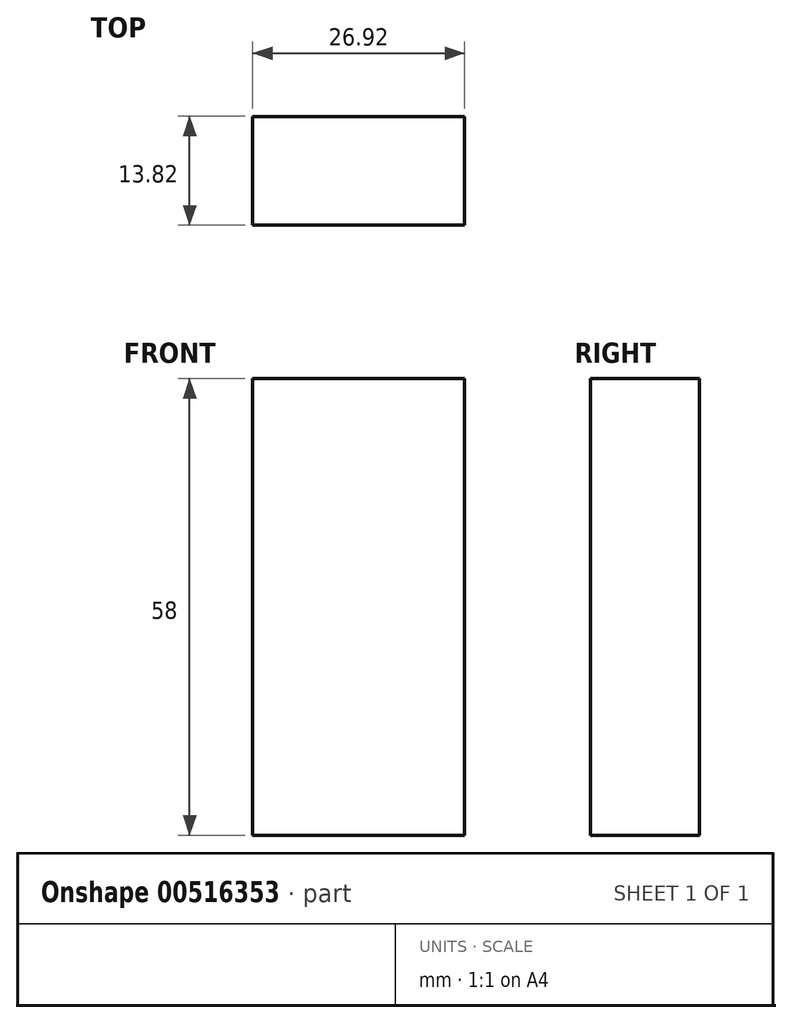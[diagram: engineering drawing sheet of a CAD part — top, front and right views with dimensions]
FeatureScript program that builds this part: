
annotation { "Feature Type Name" : "Feature", "Feature Type Description" : "" }
export const myFeature = defineFeature(function(context is Context, id is Id, definition is map)
    precondition{}
    {
        {
            var Q0;
            Q0=qCreatedBy(makeId("Top.planeOp"),FACE);
            var sketch = newSketch(context, id + "F0", { "sketchPlane" : qUnion([Q0])});
            skLineSegment(sketch, "E0.bottom", {"start": v(-34.73, 27.33) * mm, "end": v(-18.21, 27.33) * mm});
            skLineSegment(sketch, "E0.top", {"start": v(-34.73, -25.16) * mm, "end": v(-18.21, -25.16) * mm});
            skLineSegment(sketch, "E0.left", {"start": v(-34.73, 27.33) * mm, "end": v(-34.73, -25.16) * mm});
            skLineSegment(sketch, "E0.right", {"start": v(-18.21, 27.33) * mm, "end": v(-18.21, -25.16) * mm});
            skLineSegment(sketch, "E1.bottom", {"start": v(4.01, -27.84) * mm, "end": v(30.93, -27.84) * mm});
            skLineSegment(sketch, "E1.top", {"start": v(4.01, -14.02) * mm, "end": v(30.93, -14.02) * mm});
            skLineSegment(sketch, "E1.left", {"start": v(4.01, -27.84) * mm, "end": v(4.01, -14.02) * mm});
            skLineSegment(sketch, "E1.right", {"start": v(30.93, -27.84) * mm, "end": v(30.93, -14.02) * mm});
            skSolve(sketch);
        }
        {
            var Q0;
            Q0=makeQuery(id+"F0.imprint","IMPRINT",FACE,{"disambiguationData":[TD([[makeQuery(id+"F0.imprint","IMPRINT",EDGE,{"derivedFrom":sQuery(id+"F0.wireOp",EDGE,"E1.bottom")}),1.0]])]});
            extrude(context, id + "F1", {"entities" : qUnion([Q0]), "depth" : 58 * mm, "offsetDistance" : 25 * mm});
        }
    });
